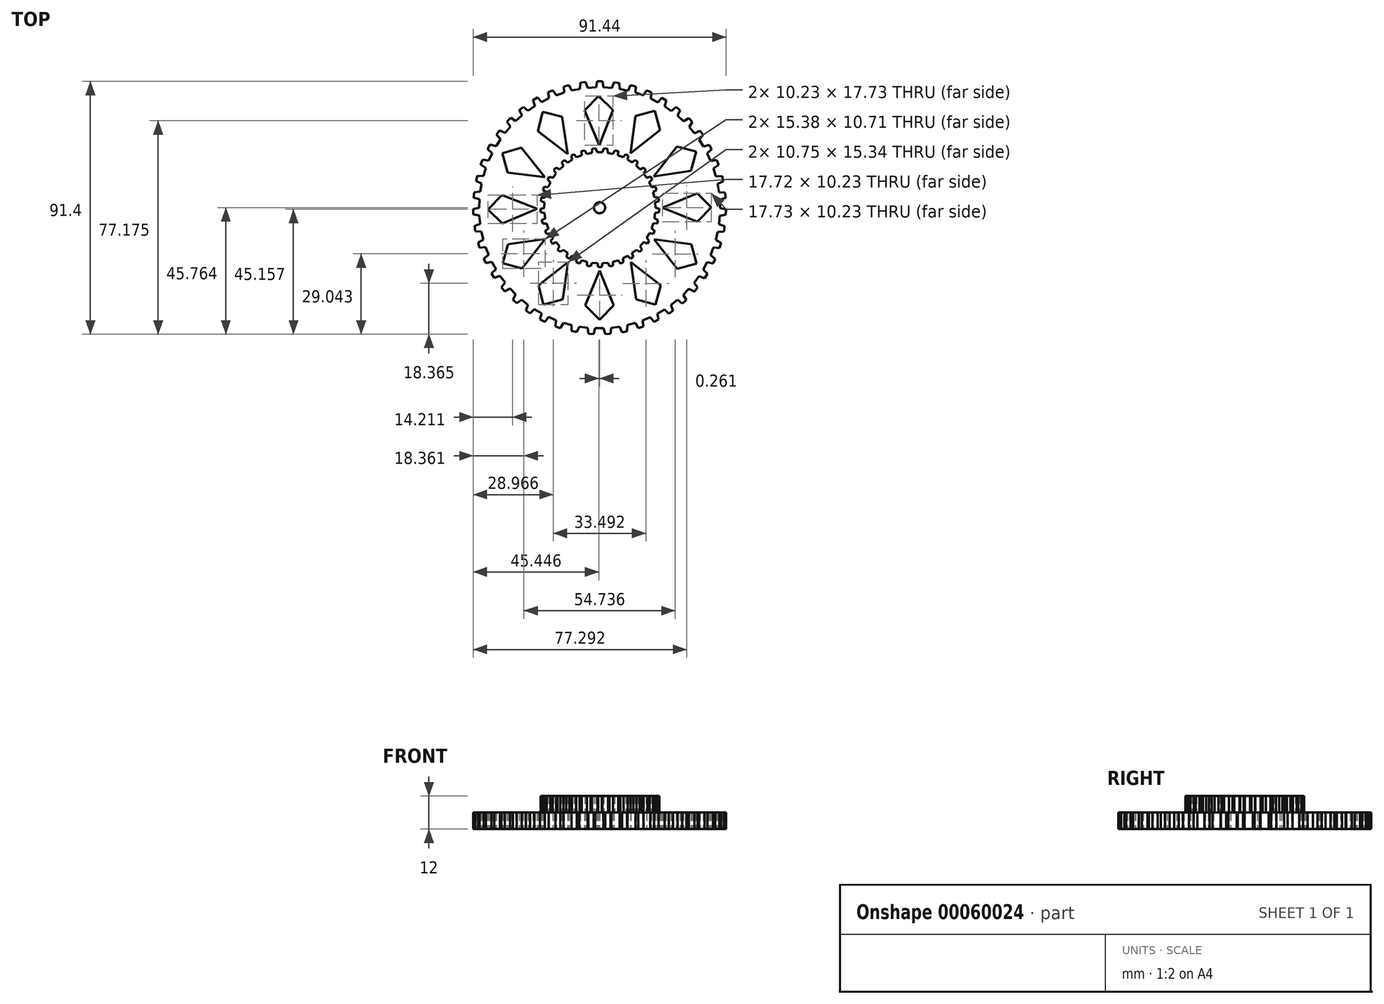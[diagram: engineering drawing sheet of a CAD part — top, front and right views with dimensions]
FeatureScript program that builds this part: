
annotation { "Feature Type Name" : "Feature", "Feature Type Description" : "" }
export const myFeature = defineFeature(function(context is Context, id is Id, definition is map)
    precondition{}
    {
        {
            var Q0;
            Q0=qCreatedBy(makeId("Top.planeOp"),FACE);
            var sketch = newSketch(context, id + "F0", { "sketchPlane" : qUnion([Q0])});
            skLineSegment(sketch, "E0", {"start": v(20.19, -0.05) * mm, "end": v(20.1, 1.94) * mm});
            skLineSegment(sketch, "E1", {"start": v(20.1, 1.94) * mm, "end": v(21.44, 2.42) * mm});
            skLineSegment(sketch, "E2", {"start": v(21.44, 2.42) * mm, "end": v(21.26, 3.68) * mm});
            skLineSegment(sketch, "E3", {"start": v(21.26, 3.68) * mm, "end": v(19.83, 3.76) * mm});
            skLineSegment(sketch, "E4", {"start": v(19.83, 3.76) * mm, "end": v(19.37, 5.7) * mm});
            skLineSegment(sketch, "E5", {"start": v(19.37, 5.7) * mm, "end": v(20.6, 6.42) * mm});
            skLineSegment(sketch, "E6", {"start": v(20.6, 6.42) * mm, "end": v(20.18, 7.62) * mm});
            skLineSegment(sketch, "E7", {"start": v(20.18, 7.62) * mm, "end": v(18.77, 7.43) * mm});
            skLineSegment(sketch, "E8", {"start": v(18.77, 7.43) * mm, "end": v(17.94, 9.24) * mm});
            skLineSegment(sketch, "E9", {"start": v(17.94, 9.24) * mm, "end": v(19, 10.18) * mm});
            skLineSegment(sketch, "E10", {"start": v(19, 10.18) * mm, "end": v(18.37, 11.28) * mm});
            skLineSegment(sketch, "E11", {"start": v(18.37, 11.28) * mm, "end": v(17.02, 10.82) * mm});
            skLineSegment(sketch, "E12", {"start": v(17.02, 10.82) * mm, "end": v(15.86, 12.44) * mm});
            skLineSegment(sketch, "E13", {"start": v(15.86, 12.44) * mm, "end": v(16.73, 13.57) * mm});
            skLineSegment(sketch, "E14", {"start": v(16.73, 13.57) * mm, "end": v(15.9, 14.53) * mm});
            skLineSegment(sketch, "E15", {"start": v(15.9, 14.53) * mm, "end": v(14.66, 13.83) * mm});
            skLineSegment(sketch, "E16", {"start": v(14.66, 13.83) * mm, "end": v(13.21, 15.2) * mm});
            skLineSegment(sketch, "E17", {"start": v(13.21, 15.2) * mm, "end": v(13.85, 16.47) * mm});
            skLineSegment(sketch, "E18", {"start": v(13.85, 16.47) * mm, "end": v(12.86, 17.26) * mm});
            skLineSegment(sketch, "E19", {"start": v(12.86, 17.26) * mm, "end": v(11.77, 16.34) * mm});
            skLineSegment(sketch, "E20", {"start": v(11.77, 16.34) * mm, "end": v(10.1, 17.41) * mm});
            skLineSegment(sketch, "E21", {"start": v(10.1, 17.41) * mm, "end": v(10.49, 18.78) * mm});
            skLineSegment(sketch, "E22", {"start": v(10.49, 18.78) * mm, "end": v(9.36, 19.36) * mm});
            skLineSegment(sketch, "E23", {"start": v(9.36, 19.36) * mm, "end": v(8.47, 18.25) * mm});
            skLineSegment(sketch, "E24", {"start": v(8.47, 18.25) * mm, "end": v(6.62, 19) * mm});
            skLineSegment(sketch, "E25", {"start": v(6.62, 19) * mm, "end": v(6.74, 20.41) * mm});
            skLineSegment(sketch, "E26", {"start": v(6.74, 20.41) * mm, "end": v(5.52, 20.77) * mm});
            skLineSegment(sketch, "E27", {"start": v(5.52, 20.77) * mm, "end": v(4.86, 19.5) * mm});
            skLineSegment(sketch, "E28", {"start": v(4.86, 19.5) * mm, "end": v(2.9, 19.88) * mm});
            skLineSegment(sketch, "E29", {"start": v(2.9, 19.88) * mm, "end": v(2.75, 21.3) * mm});
            skLineSegment(sketch, "E30", {"start": v(2.75, 21.3) * mm, "end": v(1.49, 21.41) * mm});
            skLineSegment(sketch, "E31", {"start": v(1.49, 21.41) * mm, "end": v(1.07, 20.04) * mm});
            skLineSegment(sketch, "E32", {"start": v(1.07, 20.04) * mm, "end": v(-0.92, 20.04) * mm});
            skLineSegment(sketch, "E33", {"start": v(-0.92, 20.04) * mm, "end": v(-1.33, 21.41) * mm});
            skLineSegment(sketch, "E34", {"start": v(-1.33, 21.41) * mm, "end": v(-2.6, 21.3) * mm});
            skLineSegment(sketch, "E35", {"start": v(-2.6, 21.3) * mm, "end": v(-2.74, 19.87) * mm});
            skLineSegment(sketch, "E36", {"start": v(-2.74, 19.87) * mm, "end": v(-4.7, 19.5) * mm});
            skLineSegment(sketch, "E37", {"start": v(-4.7, 19.5) * mm, "end": v(-5.36, 20.76) * mm});
            skLineSegment(sketch, "E38", {"start": v(-5.36, 20.76) * mm, "end": v(-6.58, 20.4) * mm});
            skLineSegment(sketch, "E39", {"start": v(-6.58, 20.4) * mm, "end": v(-6.46, 18.98) * mm});
            skLineSegment(sketch, "E40", {"start": v(-6.46, 18.98) * mm, "end": v(-8.3, 18.24) * mm});
            skLineSegment(sketch, "E41", {"start": v(-8.3, 18.24) * mm, "end": v(-9.2, 19.35) * mm});
            skLineSegment(sketch, "E42", {"start": v(-9.2, 19.35) * mm, "end": v(-10.33, 18.76) * mm});
            skLineSegment(sketch, "E43", {"start": v(-10.33, 18.76) * mm, "end": v(-9.93, 17.4) * mm});
            skLineSegment(sketch, "E44", {"start": v(-9.93, 17.4) * mm, "end": v(-11.6, 16.31) * mm});
            skLineSegment(sketch, "E45", {"start": v(-11.6, 16.31) * mm, "end": v(-12.7, 17.23) * mm});
            skLineSegment(sketch, "E46", {"start": v(-12.7, 17.23) * mm, "end": v(-13.7, 16.45) * mm});
            skLineSegment(sketch, "E47", {"start": v(-13.7, 16.45) * mm, "end": v(-13.05, 15.18) * mm});
            skLineSegment(sketch, "E48", {"start": v(-13.05, 15.18) * mm, "end": v(-14.49, 13.8) * mm});
            skLineSegment(sketch, "E49", {"start": v(-14.49, 13.8) * mm, "end": v(-15.73, 14.5) * mm});
            skLineSegment(sketch, "E50", {"start": v(-15.73, 14.5) * mm, "end": v(-16.56, 13.54) * mm});
            skLineSegment(sketch, "E51", {"start": v(-16.56, 13.54) * mm, "end": v(-15.69, 12.42) * mm});
            skLineSegment(sketch, "E52", {"start": v(-15.69, 12.42) * mm, "end": v(-16.84, 10.8) * mm});
            skLineSegment(sketch, "E53", {"start": v(-16.84, 10.8) * mm, "end": v(-18.2, 11.25) * mm});
            skLineSegment(sketch, "E54", {"start": v(-18.2, 11.25) * mm, "end": v(-18.83, 10.15) * mm});
            skLineSegment(sketch, "E55", {"start": v(-18.83, 10.15) * mm, "end": v(-17.76, 9.2) * mm});
            skLineSegment(sketch, "E56", {"start": v(-17.76, 9.2) * mm, "end": v(-18.59, 7.4) * mm});
            skLineSegment(sketch, "E57", {"start": v(-18.59, 7.4) * mm, "end": v(-20, 7.58) * mm});
            skLineSegment(sketch, "E58", {"start": v(-20, 7.58) * mm, "end": v(-20.41, 6.38) * mm});
            skLineSegment(sketch, "E59", {"start": v(-20.41, 6.38) * mm, "end": v(-19.18, 5.66) * mm});
            skLineSegment(sketch, "E60", {"start": v(-19.18, 5.66) * mm, "end": v(-19.65, 3.72) * mm});
            skLineSegment(sketch, "E61", {"start": v(-19.65, 3.72) * mm, "end": v(-21.08, 3.64) * mm});
            skLineSegment(sketch, "E62", {"start": v(-21.08, 3.64) * mm, "end": v(-21.25, 2.38) * mm});
            skLineSegment(sketch, "E63", {"start": v(-21.25, 2.38) * mm, "end": v(-19.9, 1.9) * mm});
            skLineSegment(sketch, "E64", {"start": v(-19.9, 1.9) * mm, "end": v(-20, -0.08) * mm});
            skLineSegment(sketch, "E65", {"start": v(-20, -0.08) * mm, "end": v(-21.38, -0.43) * mm});
            skLineSegment(sketch, "E66", {"start": v(-21.38, -0.43) * mm, "end": v(-21.32, -1.7) * mm});
            skLineSegment(sketch, "E67", {"start": v(-21.32, -1.7) * mm, "end": v(-19.9, -1.91) * mm});
            skLineSegment(sketch, "E68", {"start": v(-19.9, -1.91) * mm, "end": v(-19.62, -3.88) * mm});
            skLineSegment(sketch, "E69", {"start": v(-19.62, -3.88) * mm, "end": v(-20.92, -4.49) * mm});
            skLineSegment(sketch, "E70", {"start": v(-20.92, -4.49) * mm, "end": v(-20.62, -5.72) * mm});
            skLineSegment(sketch, "E71", {"start": v(-20.62, -5.72) * mm, "end": v(-19.2, -5.67) * mm});
            skLineSegment(sketch, "E72", {"start": v(-19.2, -5.67) * mm, "end": v(-18.54, -7.55) * mm});
            skLineSegment(sketch, "E73", {"start": v(-18.54, -7.55) * mm, "end": v(-19.7, -8.39) * mm});
            skLineSegment(sketch, "E74", {"start": v(-19.7, -8.39) * mm, "end": v(-19.17, -9.54) * mm});
            skLineSegment(sketch, "E75", {"start": v(-19.17, -9.54) * mm, "end": v(-17.78, -9.22) * mm});
            skLineSegment(sketch, "E76", {"start": v(-17.78, -9.22) * mm, "end": v(-16.78, -10.94) * mm});
            skLineSegment(sketch, "E77", {"start": v(-16.78, -10.94) * mm, "end": v(-17.75, -11.98) * mm});
            skLineSegment(sketch, "E78", {"start": v(-17.75, -11.98) * mm, "end": v(-17.01, -13.01) * mm});
            skLineSegment(sketch, "E79", {"start": v(-17.01, -13.01) * mm, "end": v(-15.71, -12.43) * mm});
            skLineSegment(sketch, "E80", {"start": v(-15.71, -12.43) * mm, "end": v(-14.4, -13.93) * mm});
            skLineSegment(sketch, "E81", {"start": v(-14.4, -13.93) * mm, "end": v(-15.17, -15.14) * mm});
            skLineSegment(sketch, "E82", {"start": v(-15.17, -15.14) * mm, "end": v(-14.25, -16.02) * mm});
            skLineSegment(sketch, "E83", {"start": v(-14.25, -16.02) * mm, "end": v(-13.08, -15.2) * mm});
            skLineSegment(sketch, "E84", {"start": v(-13.08, -15.2) * mm, "end": v(-11.51, -16.43) * mm});
            skLineSegment(sketch, "E85", {"start": v(-11.51, -16.43) * mm, "end": v(-12.03, -17.76) * mm});
            skLineSegment(sketch, "E86", {"start": v(-12.03, -17.76) * mm, "end": v(-10.96, -18.44) * mm});
            skLineSegment(sketch, "E87", {"start": v(-10.96, -18.44) * mm, "end": v(-9.97, -17.42) * mm});
            skLineSegment(sketch, "E88", {"start": v(-9.97, -17.42) * mm, "end": v(-8.2, -18.33) * mm});
            skLineSegment(sketch, "E89", {"start": v(-8.2, -18.33) * mm, "end": v(-8.46, -19.74) * mm});
            skLineSegment(sketch, "E90", {"start": v(-8.46, -19.74) * mm, "end": v(-7.28, -20.2) * mm});
            skLineSegment(sketch, "E91", {"start": v(-7.28, -20.2) * mm, "end": v(-6.5, -19.01) * mm});
            skLineSegment(sketch, "E92", {"start": v(-6.5, -19.01) * mm, "end": v(-4.59, -19.57) * mm});
            skLineSegment(sketch, "E93", {"start": v(-4.59, -19.57) * mm, "end": v(-4.57, -21) * mm});
            skLineSegment(sketch, "E94", {"start": v(-4.57, -21) * mm, "end": v(-3.32, -21.23) * mm});
            skLineSegment(sketch, "E95", {"start": v(-3.32, -21.23) * mm, "end": v(-2.78, -19.91) * mm});
            skLineSegment(sketch, "E96", {"start": v(-2.78, -19.91) * mm, "end": v(-0.8, -20.1) * mm});
            skLineSegment(sketch, "E97", {"start": v(-0.8, -20.1) * mm, "end": v(-0.52, -21.5) * mm});
            skLineSegment(sketch, "E98", {"start": v(-0.52, -21.5) * mm, "end": v(0.75, -21.5) * mm});
            skLineSegment(sketch, "E99", {"start": v(0.75, -21.5) * mm, "end": v(1.03, -20.1) * mm});
            skLineSegment(sketch, "E100", {"start": v(1.03, -20.1) * mm, "end": v(3.01, -19.9) * mm});
            skLineSegment(sketch, "E101", {"start": v(3.01, -19.9) * mm, "end": v(3.56, -21.23) * mm});
            skLineSegment(sketch, "E102", {"start": v(3.56, -21.23) * mm, "end": v(4.8, -21) * mm});
            skLineSegment(sketch, "E103", {"start": v(4.8, -21) * mm, "end": v(4.82, -19.56) * mm});
            skLineSegment(sketch, "E104", {"start": v(4.82, -19.56) * mm, "end": v(6.73, -19) * mm});
            skLineSegment(sketch, "E105", {"start": v(6.73, -19) * mm, "end": v(7.5, -20.2) * mm});
            skLineSegment(sketch, "E106", {"start": v(7.5, -20.2) * mm, "end": v(8.69, -19.72) * mm});
            skLineSegment(sketch, "E107", {"start": v(8.69, -19.72) * mm, "end": v(8.43, -18.32) * mm});
            skLineSegment(sketch, "E108", {"start": v(8.43, -18.32) * mm, "end": v(10.2, -17.4) * mm});
            skLineSegment(sketch, "E109", {"start": v(10.2, -17.4) * mm, "end": v(11.2, -18.42) * mm});
            skLineSegment(sketch, "E110", {"start": v(11.2, -18.42) * mm, "end": v(12.26, -17.74) * mm});
            skLineSegment(sketch, "E111", {"start": v(12.26, -17.74) * mm, "end": v(11.74, -16.4) * mm});
            skLineSegment(sketch, "E112", {"start": v(11.74, -16.4) * mm, "end": v(13.3, -15.17) * mm});
            skLineSegment(sketch, "E113", {"start": v(13.3, -15.17) * mm, "end": v(14.47, -15.99) * mm});
            skLineSegment(sketch, "E114", {"start": v(14.47, -15.99) * mm, "end": v(15.39, -15.11) * mm});
            skLineSegment(sketch, "E115", {"start": v(15.39, -15.11) * mm, "end": v(14.63, -13.9) * mm});
            skLineSegment(sketch, "E116", {"start": v(14.63, -13.9) * mm, "end": v(15.93, -12.4) * mm});
            skLineSegment(sketch, "E117", {"start": v(15.93, -12.4) * mm, "end": v(17.23, -12.98) * mm});
            skLineSegment(sketch, "E118", {"start": v(17.23, -12.98) * mm, "end": v(17.97, -11.95) * mm});
            skLineSegment(sketch, "E119", {"start": v(17.97, -11.95) * mm, "end": v(17, -10.9) * mm});
            skLineSegment(sketch, "E120", {"start": v(17, -10.9) * mm, "end": v(18, -9.18) * mm});
            skLineSegment(sketch, "E121", {"start": v(18, -9.18) * mm, "end": v(19.38, -9.5) * mm});
            skLineSegment(sketch, "E122", {"start": v(19.38, -9.5) * mm, "end": v(19.9, -8.35) * mm});
            skLineSegment(sketch, "E123", {"start": v(19.9, -8.35) * mm, "end": v(18.75, -7.51) * mm});
            skLineSegment(sketch, "E124", {"start": v(18.75, -7.51) * mm, "end": v(19.4, -5.63) * mm});
            skLineSegment(sketch, "E125", {"start": v(19.4, -5.63) * mm, "end": v(20.83, -5.69) * mm});
            skLineSegment(sketch, "E126", {"start": v(20.83, -5.69) * mm, "end": v(21.12, -4.45) * mm});
            skLineSegment(sketch, "E127", {"start": v(21.12, -4.45) * mm, "end": v(19.83, -3.85) * mm});
            skLineSegment(sketch, "E128", {"start": v(19.83, -3.85) * mm, "end": v(20.1, -1.88) * mm});
            skLineSegment(sketch, "E129", {"start": v(20.1, -1.88) * mm, "end": v(21.52, -1.66) * mm});
            skLineSegment(sketch, "E130", {"start": v(21.52, -1.66) * mm, "end": v(21.58, -0.4) * mm});
            skLineSegment(sketch, "E131", {"start": v(21.58, -0.4) * mm, "end": v(20.19, -0.05) * mm});
            skLineSegment(sketch, "E132", {"start": v(-22.65, -0.36) * mm, "end": v(-35.18, -5.66) * mm});
            skLineSegment(sketch, "E133", {"start": v(-35.18, -5.66) * mm, "end": v(-40.37, -0.62) * mm});
            skLineSegment(sketch, "E134", {"start": v(-40.37, -0.62) * mm, "end": v(-35.33, 4.57) * mm});
            skLineSegment(sketch, "E135", {"start": v(-35.33, 4.57) * mm, "end": v(-22.65, -0.36) * mm});
            skLineSegment(sketch, "E136", {"start": v(-19.74, 11.05) * mm, "end": v(-33.24, 12.75) * mm});
            skLineSegment(sketch, "E137", {"start": v(-33.24, 12.75) * mm, "end": v(-35.2, 19.71) * mm});
            skLineSegment(sketch, "E138", {"start": v(-35.2, 19.71) * mm, "end": v(-28.24, 21.68) * mm});
            skLineSegment(sketch, "E139", {"start": v(-28.24, 21.68) * mm, "end": v(-19.74, 11.05) * mm});
            skLineSegment(sketch, "E140", {"start": v(-11.5, 19.47) * mm, "end": v(-22.33, 27.7) * mm});
            skLineSegment(sketch, "E141", {"start": v(-22.33, 27.7) * mm, "end": v(-20.54, 34.71) * mm});
            skLineSegment(sketch, "E142", {"start": v(-20.54, 34.71) * mm, "end": v(-13.53, 32.92) * mm});
            skLineSegment(sketch, "E143", {"start": v(-13.53, 32.92) * mm, "end": v(-11.5, 19.47) * mm});
            skLineSegment(sketch, "E144", {"start": v(-0.15, 22.61) * mm, "end": v(-5.39, 35.17) * mm});
            skLineSegment(sketch, "E145", {"start": v(-5.39, 35.17) * mm, "end": v(-0.32, 40.34) * mm});
            skLineSegment(sketch, "E146", {"start": v(-0.32, 40.34) * mm, "end": v(4.84, 35.28) * mm});
            skLineSegment(sketch, "E147", {"start": v(4.84, 35.28) * mm, "end": v(-0.15, 22.61) * mm});
            skLineSegment(sketch, "E148", {"start": v(11.25, 19.64) * mm, "end": v(13.01, 33.14) * mm});
            skLineSegment(sketch, "E149", {"start": v(13.01, 33.14) * mm, "end": v(19.98, 35.07) * mm});
            skLineSegment(sketch, "E150", {"start": v(19.98, 35.07) * mm, "end": v(21.91, 28.1) * mm});
            skLineSegment(sketch, "E151", {"start": v(21.91, 28.1) * mm, "end": v(11.25, 19.64) * mm});
            skLineSegment(sketch, "E152", {"start": v(19.62, 11.36) * mm, "end": v(27.91, 22.15) * mm});
            skLineSegment(sketch, "E153", {"start": v(27.91, 22.15) * mm, "end": v(34.91, 20.33) * mm});
            skLineSegment(sketch, "E154", {"start": v(34.91, 20.33) * mm, "end": v(33.09, 13.33) * mm});
            skLineSegment(sketch, "E155", {"start": v(33.09, 13.33) * mm, "end": v(19.62, 11.36) * mm});
            skLineSegment(sketch, "E156", {"start": v(22.7, 0) * mm, "end": v(35.3, 5.18) * mm});
            skLineSegment(sketch, "E157", {"start": v(35.3, 5.18) * mm, "end": v(40.44, 0.1) * mm});
            skLineSegment(sketch, "E158", {"start": v(40.44, 0.1) * mm, "end": v(35.35, -5.05) * mm});
            skLineSegment(sketch, "E159", {"start": v(35.35, -5.05) * mm, "end": v(22.7, 0) * mm});
            skLineSegment(sketch, "E160", {"start": v(19.69, -11.38) * mm, "end": v(33.17, -13.21) * mm});
            skLineSegment(sketch, "E161", {"start": v(33.17, -13.21) * mm, "end": v(35.07, -20.2) * mm});
            skLineSegment(sketch, "E162", {"start": v(35.07, -20.2) * mm, "end": v(28.09, -22.09) * mm});
            skLineSegment(sketch, "E163", {"start": v(28.09, -22.09) * mm, "end": v(19.69, -11.38) * mm});
            skLineSegment(sketch, "E164", {"start": v(11.36, -19.71) * mm, "end": v(22.11, -28.06) * mm});
            skLineSegment(sketch, "E165", {"start": v(22.11, -28.06) * mm, "end": v(20.25, -35.05) * mm});
            skLineSegment(sketch, "E166", {"start": v(20.25, -35.05) * mm, "end": v(13.26, -33.19) * mm});
            skLineSegment(sketch, "E167", {"start": v(13.26, -33.19) * mm, "end": v(11.36, -19.71) * mm});
            skLineSegment(sketch, "E168", {"start": v(-0.01, -22.75) * mm, "end": v(5.1, -35.36) * mm});
            skLineSegment(sketch, "E169", {"start": v(5.1, -35.36) * mm, "end": v(-0.01, -40.47) * mm});
            skLineSegment(sketch, "E170", {"start": v(-0.01, -40.47) * mm, "end": v(-5.13, -35.36) * mm});
            skLineSegment(sketch, "E171", {"start": v(-5.13, -35.36) * mm, "end": v(-0.01, -22.75) * mm});
            skLineSegment(sketch, "E172", {"start": v(-11.38, -19.67) * mm, "end": v(-13.28, -33.14) * mm});
            skLineSegment(sketch, "E173", {"start": v(-13.28, -33.14) * mm, "end": v(-20.27, -35) * mm});
            skLineSegment(sketch, "E174", {"start": v(-20.27, -35) * mm, "end": v(-22.13, -28.02) * mm});
            skLineSegment(sketch, "E175", {"start": v(-22.13, -28.02) * mm, "end": v(-11.38, -19.67) * mm});
            skLineSegment(sketch, "E176", {"start": v(-19.67, -11.3) * mm, "end": v(-28.07, -22.01) * mm});
            skLineSegment(sketch, "E177", {"start": v(-28.07, -22.01) * mm, "end": v(-35.05, -20.12) * mm});
            skLineSegment(sketch, "E178", {"start": v(-35.05, -20.12) * mm, "end": v(-33.16, -13.14) * mm});
            skLineSegment(sketch, "E179", {"start": v(-33.16, -13.14) * mm, "end": v(-19.67, -11.3) * mm});
            skLineSegment(sketch, "E180", {"start": v(43.6, -0.15) * mm, "end": v(43.5, 2.88) * mm});
            skLineSegment(sketch, "E181", {"start": v(43.5, 2.88) * mm, "end": v(45.6, 3.54) * mm});
            skLineSegment(sketch, "E182", {"start": v(45.6, 3.54) * mm, "end": v(45.41, 5.42) * mm});
            skLineSegment(sketch, "E183", {"start": v(45.41, 5.42) * mm, "end": v(43.23, 5.66) * mm});
            skLineSegment(sketch, "E184", {"start": v(43.23, 5.66) * mm, "end": v(42.73, 8.66) * mm});
            skLineSegment(sketch, "E185", {"start": v(42.73, 8.66) * mm, "end": v(44.72, 9.58) * mm});
            skLineSegment(sketch, "E186", {"start": v(44.72, 9.58) * mm, "end": v(44.28, 11.43) * mm});
            skLineSegment(sketch, "E187", {"start": v(44.28, 11.43) * mm, "end": v(42.1, 11.37) * mm});
            skLineSegment(sketch, "E188", {"start": v(42.1, 11.37) * mm, "end": v(41.2, 14.28) * mm});
            skLineSegment(sketch, "E189", {"start": v(41.2, 14.28) * mm, "end": v(43.04, 15.46) * mm});
            skLineSegment(sketch, "E190", {"start": v(43.04, 15.46) * mm, "end": v(42.36, 17.23) * mm});
            skLineSegment(sketch, "E191", {"start": v(42.36, 17.23) * mm, "end": v(40.2, 16.88) * mm});
            skLineSegment(sketch, "E192", {"start": v(40.2, 16.88) * mm, "end": v(38.92, 19.63) * mm});
            skLineSegment(sketch, "E193", {"start": v(38.92, 19.63) * mm, "end": v(40.59, 21.06) * mm});
            skLineSegment(sketch, "E194", {"start": v(40.59, 21.06) * mm, "end": v(39.68, 22.72) * mm});
            skLineSegment(sketch, "E195", {"start": v(39.68, 22.72) * mm, "end": v(37.59, 22.08) * mm});
            skLineSegment(sketch, "E196", {"start": v(37.59, 22.08) * mm, "end": v(35.95, 24.64) * mm});
            skLineSegment(sketch, "E197", {"start": v(35.95, 24.64) * mm, "end": v(37.42, 26.28) * mm});
            skLineSegment(sketch, "E198", {"start": v(37.42, 26.28) * mm, "end": v(36.3, 27.8) * mm});
            skLineSegment(sketch, "E199", {"start": v(36.3, 27.8) * mm, "end": v(34.3, 26.9) * mm});
            skLineSegment(sketch, "E200", {"start": v(34.3, 26.9) * mm, "end": v(32.34, 29.21) * mm});
            skLineSegment(sketch, "E201", {"start": v(32.34, 29.21) * mm, "end": v(33.58, 31.03) * mm});
            skLineSegment(sketch, "E202", {"start": v(33.58, 31.03) * mm, "end": v(32.26, 32.39) * mm});
            skLineSegment(sketch, "E203", {"start": v(32.26, 32.39) * mm, "end": v(30.4, 31.22) * mm});
            skLineSegment(sketch, "E204", {"start": v(30.4, 31.22) * mm, "end": v(28.15, 33.26) * mm});
            skLineSegment(sketch, "E205", {"start": v(28.15, 33.26) * mm, "end": v(29.14, 35.22) * mm});
            skLineSegment(sketch, "E206", {"start": v(29.14, 35.22) * mm, "end": v(27.65, 36.4) * mm});
            skLineSegment(sketch, "E207", {"start": v(27.65, 36.4) * mm, "end": v(25.97, 35) * mm});
            skLineSegment(sketch, "E208", {"start": v(25.97, 35) * mm, "end": v(23.47, 36.72) * mm});
            skLineSegment(sketch, "E209", {"start": v(23.47, 36.72) * mm, "end": v(24.18, 38.8) * mm});
            skLineSegment(sketch, "E210", {"start": v(24.18, 38.8) * mm, "end": v(22.55, 39.76) * mm});
            skLineSegment(sketch, "E211", {"start": v(22.55, 39.76) * mm, "end": v(21.07, 38.15) * mm});
            skLineSegment(sketch, "E212", {"start": v(21.07, 38.15) * mm, "end": v(18.37, 39.53) * mm});
            skLineSegment(sketch, "E213", {"start": v(18.37, 39.53) * mm, "end": v(18.8, 41.67) * mm});
            skLineSegment(sketch, "E214", {"start": v(18.8, 41.67) * mm, "end": v(17.05, 42.42) * mm});
            skLineSegment(sketch, "E215", {"start": v(17.05, 42.42) * mm, "end": v(15.8, 40.62) * mm});
            skLineSegment(sketch, "E216", {"start": v(15.8, 40.62) * mm, "end": v(12.93, 41.62) * mm});
            skLineSegment(sketch, "E217", {"start": v(12.93, 41.62) * mm, "end": v(13.07, 43.82) * mm});
            skLineSegment(sketch, "E218", {"start": v(13.07, 43.82) * mm, "end": v(11.24, 44.31) * mm});
            skLineSegment(sketch, "E219", {"start": v(11.24, 44.31) * mm, "end": v(10.24, 42.36) * mm});
            skLineSegment(sketch, "E220", {"start": v(10.24, 42.36) * mm, "end": v(7.26, 42.97) * mm});
            skLineSegment(sketch, "E221", {"start": v(7.26, 42.97) * mm, "end": v(7.1, 45.15) * mm});
            skLineSegment(sketch, "E222", {"start": v(7.1, 45.15) * mm, "end": v(5.23, 45.4) * mm});
            skLineSegment(sketch, "E223", {"start": v(5.23, 45.4) * mm, "end": v(4.5, 43.34) * mm});
            skLineSegment(sketch, "E224", {"start": v(4.5, 43.34) * mm, "end": v(1.47, 43.55) * mm});
            skLineSegment(sketch, "E225", {"start": v(1.47, 43.55) * mm, "end": v(1.02, 45.69) * mm});
            skLineSegment(sketch, "E226", {"start": v(1.02, 45.69) * mm, "end": v(-0.87, 45.7) * mm});
            skLineSegment(sketch, "E227", {"start": v(-0.87, 45.7) * mm, "end": v(-1.32, 43.55) * mm});
            skLineSegment(sketch, "E228", {"start": v(-1.32, 43.55) * mm, "end": v(-4.35, 43.35) * mm});
            skLineSegment(sketch, "E229", {"start": v(-4.35, 43.35) * mm, "end": v(-5.08, 45.43) * mm});
            skLineSegment(sketch, "E230", {"start": v(-5.08, 45.43) * mm, "end": v(-6.95, 45.17) * mm});
            skLineSegment(sketch, "E231", {"start": v(-6.95, 45.17) * mm, "end": v(-7.12, 42.99) * mm});
            skLineSegment(sketch, "E232", {"start": v(-7.12, 42.99) * mm, "end": v(-10.1, 42.4) * mm});
            skLineSegment(sketch, "E233", {"start": v(-10.1, 42.4) * mm, "end": v(-11.09, 44.34) * mm});
            skLineSegment(sketch, "E234", {"start": v(-11.09, 44.34) * mm, "end": v(-12.92, 43.84) * mm});
            skLineSegment(sketch, "E235", {"start": v(-12.92, 43.84) * mm, "end": v(-12.79, 41.66) * mm});
            skLineSegment(sketch, "E236", {"start": v(-12.79, 41.66) * mm, "end": v(-15.66, 40.67) * mm});
            skLineSegment(sketch, "E237", {"start": v(-15.66, 40.67) * mm, "end": v(-16.9, 42.47) * mm});
            skLineSegment(sketch, "E238", {"start": v(-16.9, 42.47) * mm, "end": v(-18.65, 41.74) * mm});
            skLineSegment(sketch, "E239", {"start": v(-18.65, 41.74) * mm, "end": v(-18.23, 39.58) * mm});
            skLineSegment(sketch, "E240", {"start": v(-18.23, 39.58) * mm, "end": v(-20.94, 38.21) * mm});
            skLineSegment(sketch, "E241", {"start": v(-20.94, 38.21) * mm, "end": v(-22.42, 39.84) * mm});
            skLineSegment(sketch, "E242", {"start": v(-22.42, 39.84) * mm, "end": v(-24.05, 38.87) * mm});
            skLineSegment(sketch, "E243", {"start": v(-24.05, 38.87) * mm, "end": v(-23.34, 36.8) * mm});
            skLineSegment(sketch, "E244", {"start": v(-23.34, 36.8) * mm, "end": v(-25.85, 35.08) * mm});
            skLineSegment(sketch, "E245", {"start": v(-25.85, 35.08) * mm, "end": v(-27.53, 36.49) * mm});
            skLineSegment(sketch, "E246", {"start": v(-27.53, 36.49) * mm, "end": v(-29.01, 35.31) * mm});
            skLineSegment(sketch, "E247", {"start": v(-29.01, 35.31) * mm, "end": v(-28.04, 33.35) * mm});
            skLineSegment(sketch, "E248", {"start": v(-28.04, 33.35) * mm, "end": v(-30.3, 31.32) * mm});
            skLineSegment(sketch, "E249", {"start": v(-30.3, 31.32) * mm, "end": v(-32.14, 32.49) * mm});
            skLineSegment(sketch, "E250", {"start": v(-32.14, 32.49) * mm, "end": v(-33.46, 31.13) * mm});
            skLineSegment(sketch, "E251", {"start": v(-33.46, 31.13) * mm, "end": v(-32.24, 29.31) * mm});
            skLineSegment(sketch, "E252", {"start": v(-32.24, 29.31) * mm, "end": v(-34.2, 27) * mm});
            skLineSegment(sketch, "E253", {"start": v(-34.2, 27) * mm, "end": v(-36.19, 27.91) * mm});
            skLineSegment(sketch, "E254", {"start": v(-36.19, 27.91) * mm, "end": v(-37.32, 26.4) * mm});
            skLineSegment(sketch, "E255", {"start": v(-37.32, 26.4) * mm, "end": v(-35.86, 24.76) * mm});
            skLineSegment(sketch, "E256", {"start": v(-35.86, 24.76) * mm, "end": v(-37.5, 22.2) * mm});
            skLineSegment(sketch, "E257", {"start": v(-37.5, 22.2) * mm, "end": v(-39.6, 22.85) * mm});
            skLineSegment(sketch, "E258", {"start": v(-39.6, 22.85) * mm, "end": v(-40.52, 21.19) * mm});
            skLineSegment(sketch, "E259", {"start": v(-40.52, 21.19) * mm, "end": v(-38.85, 19.76) * mm});
            skLineSegment(sketch, "E260", {"start": v(-38.85, 19.76) * mm, "end": v(-40.13, 17) * mm});
            skLineSegment(sketch, "E261", {"start": v(-40.13, 17) * mm, "end": v(-42.3, 17.36) * mm});
            skLineSegment(sketch, "E262", {"start": v(-42.3, 17.36) * mm, "end": v(-42.98, 15.6) * mm});
            skLineSegment(sketch, "E263", {"start": v(-42.98, 15.6) * mm, "end": v(-41.14, 14.4) * mm});
            skLineSegment(sketch, "E264", {"start": v(-41.14, 14.4) * mm, "end": v(-42.05, 11.5) * mm});
            skLineSegment(sketch, "E265", {"start": v(-42.05, 11.5) * mm, "end": v(-44.23, 11.57) * mm});
            skLineSegment(sketch, "E266", {"start": v(-44.23, 11.57) * mm, "end": v(-44.67, 9.72) * mm});
            skLineSegment(sketch, "E267", {"start": v(-44.67, 9.72) * mm, "end": v(-42.7, 8.79) * mm});
            skLineSegment(sketch, "E268", {"start": v(-42.7, 8.79) * mm, "end": v(-43.2, 5.8) * mm});
            skLineSegment(sketch, "E269", {"start": v(-43.2, 5.8) * mm, "end": v(-45.38, 5.57) * mm});
            skLineSegment(sketch, "E270", {"start": v(-45.38, 5.57) * mm, "end": v(-45.57, 3.68) * mm});
            skLineSegment(sketch, "E271", {"start": v(-45.57, 3.68) * mm, "end": v(-43.48, 3.02) * mm});
            skLineSegment(sketch, "E272", {"start": v(-43.48, 3.02) * mm, "end": v(-43.58, -0.02) * mm});
            skLineSegment(sketch, "E273", {"start": v(-43.58, -0.02) * mm, "end": v(-45.72, -0.53) * mm});
            skLineSegment(sketch, "E274", {"start": v(-45.72, -0.53) * mm, "end": v(-45.65, -2.43) * mm});
            skLineSegment(sketch, "E275", {"start": v(-45.65, -2.43) * mm, "end": v(-43.5, -2.8) * mm});
            skLineSegment(sketch, "E276", {"start": v(-43.5, -2.8) * mm, "end": v(-43.2, -5.83) * mm});
            skLineSegment(sketch, "E277", {"start": v(-43.2, -5.83) * mm, "end": v(-45.24, -6.62) * mm});
            skLineSegment(sketch, "E278", {"start": v(-45.24, -6.62) * mm, "end": v(-44.93, -8.49) * mm});
            skLineSegment(sketch, "E279", {"start": v(-44.93, -8.49) * mm, "end": v(-42.74, -8.58) * mm});
            skLineSegment(sketch, "E280", {"start": v(-42.74, -8.58) * mm, "end": v(-42.05, -11.54) * mm});
            skLineSegment(sketch, "E281", {"start": v(-42.05, -11.54) * mm, "end": v(-43.97, -12.6) * mm});
            skLineSegment(sketch, "E282", {"start": v(-43.97, -12.6) * mm, "end": v(-43.41, -14.4) * mm});
            skLineSegment(sketch, "E283", {"start": v(-43.41, -14.4) * mm, "end": v(-41.23, -14.2) * mm});
            skLineSegment(sketch, "E284", {"start": v(-41.23, -14.2) * mm, "end": v(-40.14, -17.04) * mm});
            skLineSegment(sketch, "E285", {"start": v(-40.14, -17.04) * mm, "end": v(-41.9, -18.35) * mm});
            skLineSegment(sketch, "E286", {"start": v(-41.9, -18.35) * mm, "end": v(-41.1, -20.07) * mm});
            skLineSegment(sketch, "E287", {"start": v(-41.1, -20.07) * mm, "end": v(-38.97, -19.57) * mm});
            skLineSegment(sketch, "E288", {"start": v(-38.97, -19.57) * mm, "end": v(-37.51, -22.24) * mm});
            skLineSegment(sketch, "E289", {"start": v(-37.51, -22.24) * mm, "end": v(-39.08, -23.77) * mm});
            skLineSegment(sketch, "E290", {"start": v(-39.08, -23.77) * mm, "end": v(-38.06, -25.36) * mm});
            skLineSegment(sketch, "E291", {"start": v(-38.06, -25.36) * mm, "end": v(-36, -24.59) * mm});
            skLineSegment(sketch, "E292", {"start": v(-36, -24.59) * mm, "end": v(-34.2, -27.03) * mm});
            skLineSegment(sketch, "E293", {"start": v(-34.2, -27.03) * mm, "end": v(-35.56, -28.76) * mm});
            skLineSegment(sketch, "E294", {"start": v(-35.56, -28.76) * mm, "end": v(-34.34, -30.2) * mm});
            skLineSegment(sketch, "E295", {"start": v(-34.34, -30.2) * mm, "end": v(-32.41, -29.17) * mm});
            skLineSegment(sketch, "E296", {"start": v(-32.41, -29.17) * mm, "end": v(-30.3, -31.35) * mm});
            skLineSegment(sketch, "E297", {"start": v(-30.3, -31.35) * mm, "end": v(-31.41, -33.24) * mm});
            skLineSegment(sketch, "E298", {"start": v(-31.41, -33.24) * mm, "end": v(-30.01, -34.52) * mm});
            skLineSegment(sketch, "E299", {"start": v(-30.01, -34.52) * mm, "end": v(-28.24, -33.23) * mm});
            skLineSegment(sketch, "E300", {"start": v(-28.24, -33.23) * mm, "end": v(-25.86, -35.11) * mm});
            skLineSegment(sketch, "E301", {"start": v(-25.86, -35.11) * mm, "end": v(-26.71, -37.14) * mm});
            skLineSegment(sketch, "E302", {"start": v(-26.71, -37.14) * mm, "end": v(-25.15, -38.22) * mm});
            skLineSegment(sketch, "E303", {"start": v(-25.15, -38.22) * mm, "end": v(-23.56, -36.7) * mm});
            skLineSegment(sketch, "E304", {"start": v(-23.56, -36.7) * mm, "end": v(-20.95, -38.25) * mm});
            skLineSegment(sketch, "E305", {"start": v(-20.95, -38.25) * mm, "end": v(-21.53, -40.37) * mm});
            skLineSegment(sketch, "E306", {"start": v(-21.53, -40.37) * mm, "end": v(-19.83, -41.23) * mm});
            skLineSegment(sketch, "E307", {"start": v(-19.83, -41.23) * mm, "end": v(-18.46, -39.52) * mm});
            skLineSegment(sketch, "E308", {"start": v(-18.46, -39.52) * mm, "end": v(-15.67, -40.7) * mm});
            skLineSegment(sketch, "E309", {"start": v(-15.67, -40.7) * mm, "end": v(-15.95, -42.88) * mm});
            skLineSegment(sketch, "E310", {"start": v(-15.95, -42.88) * mm, "end": v(-14.16, -43.5) * mm});
            skLineSegment(sketch, "E311", {"start": v(-14.16, -43.5) * mm, "end": v(-13.04, -41.63) * mm});
            skLineSegment(sketch, "E312", {"start": v(-13.04, -41.63) * mm, "end": v(-10.1, -42.43) * mm});
            skLineSegment(sketch, "E313", {"start": v(-10.1, -42.43) * mm, "end": v(-10.1, -44.62) * mm});
            skLineSegment(sketch, "E314", {"start": v(-10.1, -44.62) * mm, "end": v(-8.24, -45) * mm});
            skLineSegment(sketch, "E315", {"start": v(-8.24, -45) * mm, "end": v(-7.37, -43) * mm});
            skLineSegment(sketch, "E316", {"start": v(-7.37, -43) * mm, "end": v(-4.36, -43.4) * mm});
            skLineSegment(sketch, "E317", {"start": v(-4.36, -43.4) * mm, "end": v(-4.06, -45.58) * mm});
            skLineSegment(sketch, "E318", {"start": v(-4.06, -45.58) * mm, "end": v(-2.17, -45.7) * mm});
            skLineSegment(sketch, "E319", {"start": v(-2.17, -45.7) * mm, "end": v(-1.58, -43.59) * mm});
            skLineSegment(sketch, "E320", {"start": v(-1.58, -43.59) * mm, "end": v(1.46, -43.59) * mm});
            skLineSegment(sketch, "E321", {"start": v(1.46, -43.59) * mm, "end": v(2.04, -45.7) * mm});
            skLineSegment(sketch, "E322", {"start": v(2.04, -45.7) * mm, "end": v(3.93, -45.58) * mm});
            skLineSegment(sketch, "E323", {"start": v(3.93, -45.58) * mm, "end": v(4.24, -43.4) * mm});
            skLineSegment(sketch, "E324", {"start": v(4.24, -43.4) * mm, "end": v(7.25, -43.02) * mm});
            skLineSegment(sketch, "E325", {"start": v(7.25, -43.02) * mm, "end": v(8.11, -45.03) * mm});
            skLineSegment(sketch, "E326", {"start": v(8.11, -45.03) * mm, "end": v(9.97, -44.66) * mm});
            skLineSegment(sketch, "E327", {"start": v(9.97, -44.66) * mm, "end": v(9.99, -42.46) * mm});
            skLineSegment(sketch, "E328", {"start": v(9.99, -42.46) * mm, "end": v(12.92, -41.67) * mm});
            skLineSegment(sketch, "E329", {"start": v(12.92, -41.67) * mm, "end": v(14.04, -43.56) * mm});
            skLineSegment(sketch, "E330", {"start": v(14.04, -43.56) * mm, "end": v(15.83, -42.93) * mm});
            skLineSegment(sketch, "E331", {"start": v(15.83, -42.93) * mm, "end": v(15.56, -40.76) * mm});
            skLineSegment(sketch, "E332", {"start": v(15.56, -40.76) * mm, "end": v(18.35, -39.58) * mm});
            skLineSegment(sketch, "E333", {"start": v(18.35, -39.58) * mm, "end": v(19.72, -41.29) * mm});
            skLineSegment(sketch, "E334", {"start": v(19.72, -41.29) * mm, "end": v(21.41, -40.43) * mm});
            skLineSegment(sketch, "E335", {"start": v(21.41, -40.43) * mm, "end": v(20.85, -38.32) * mm});
            skLineSegment(sketch, "E336", {"start": v(20.85, -38.32) * mm, "end": v(23.46, -36.77) * mm});
            skLineSegment(sketch, "E337", {"start": v(23.46, -36.77) * mm, "end": v(25.04, -38.29) * mm});
            skLineSegment(sketch, "E338", {"start": v(25.04, -38.29) * mm, "end": v(26.6, -37.22) * mm});
            skLineSegment(sketch, "E339", {"start": v(26.6, -37.22) * mm, "end": v(25.76, -35.2) * mm});
            skLineSegment(sketch, "E340", {"start": v(25.76, -35.2) * mm, "end": v(28.15, -33.32) * mm});
            skLineSegment(sketch, "E341", {"start": v(28.15, -33.32) * mm, "end": v(29.92, -34.6) * mm});
            skLineSegment(sketch, "E342", {"start": v(29.92, -34.6) * mm, "end": v(31.33, -33.34) * mm});
            skLineSegment(sketch, "E343", {"start": v(31.33, -33.34) * mm, "end": v(30.22, -31.45) * mm});
            skLineSegment(sketch, "E344", {"start": v(30.22, -31.45) * mm, "end": v(32.33, -29.27) * mm});
            skLineSegment(sketch, "E345", {"start": v(32.33, -29.27) * mm, "end": v(34.26, -30.32) * mm});
            skLineSegment(sketch, "E346", {"start": v(34.26, -30.32) * mm, "end": v(35.49, -28.87) * mm});
            skLineSegment(sketch, "E347", {"start": v(35.49, -28.87) * mm, "end": v(34.14, -27.14) * mm});
            skLineSegment(sketch, "E348", {"start": v(34.14, -27.14) * mm, "end": v(35.95, -24.7) * mm});
            skLineSegment(sketch, "E349", {"start": v(35.95, -24.7) * mm, "end": v(38, -25.48) * mm});
            skLineSegment(sketch, "E350", {"start": v(38, -25.48) * mm, "end": v(39.01, -23.88) * mm});
            skLineSegment(sketch, "E351", {"start": v(39.01, -23.88) * mm, "end": v(37.45, -22.35) * mm});
            skLineSegment(sketch, "E352", {"start": v(37.45, -22.35) * mm, "end": v(38.92, -19.7) * mm});
            skLineSegment(sketch, "E353", {"start": v(38.92, -19.7) * mm, "end": v(41.05, -20.2) * mm});
            skLineSegment(sketch, "E354", {"start": v(41.05, -20.2) * mm, "end": v(41.85, -18.47) * mm});
            skLineSegment(sketch, "E355", {"start": v(41.85, -18.47) * mm, "end": v(40.1, -17.16) * mm});
            skLineSegment(sketch, "E356", {"start": v(40.1, -17.16) * mm, "end": v(41.2, -14.33) * mm});
            skLineSegment(sketch, "E357", {"start": v(41.2, -14.33) * mm, "end": v(43.37, -14.54) * mm});
            skLineSegment(sketch, "E358", {"start": v(43.37, -14.54) * mm, "end": v(43.94, -12.73) * mm});
            skLineSegment(sketch, "E359", {"start": v(43.94, -12.73) * mm, "end": v(42.02, -11.67) * mm});
            skLineSegment(sketch, "E360", {"start": v(42.02, -11.67) * mm, "end": v(42.73, -8.71) * mm});
            skLineSegment(sketch, "E361", {"start": v(42.73, -8.71) * mm, "end": v(44.93, -8.63) * mm});
            skLineSegment(sketch, "E362", {"start": v(44.93, -8.63) * mm, "end": v(45.24, -6.76) * mm});
            skLineSegment(sketch, "E363", {"start": v(45.24, -6.76) * mm, "end": v(43.2, -5.96) * mm});
            skLineSegment(sketch, "E364", {"start": v(43.2, -5.96) * mm, "end": v(43.5, -2.94) * mm});
            skLineSegment(sketch, "E365", {"start": v(43.5, -2.94) * mm, "end": v(45.66, -2.57) * mm});
            skLineSegment(sketch, "E366", {"start": v(45.66, -2.57) * mm, "end": v(45.72, -0.67) * mm});
            skLineSegment(sketch, "E367", {"start": v(45.72, -0.67) * mm, "end": v(43.6, -0.15) * mm});
            skPoint(sketch, "E368", {"position": v(0, 0) * mm});
            skCircle(sketch, "E369", {"center": v(0, 0) * mm, "radius": 0.72 * mm});
            skSolve(sketch);
        }
        {
            var Q0;
            Q0=makeQuery(id+"F0.imprint","IMPRINT",FACE,{"disambiguationData":[TD([[makeQuery(id+"F0.imprint","IMPRINT",EDGE,{"derivedFrom":sQuery(id+"F0.wireOp",EDGE,"E0")}),-1.0]])]});
            var Q1;
            Q1=makeQuery(id+"F0.imprint","IMPRINT",FACE,{"disambiguationData":[TD([[makeQuery(id+"F0.imprint","IMPRINT",EDGE,{"derivedFrom":sQuery(id+"F0.wireOp",EDGE,"E0")}),1.0]])]});
            extrude(context, id + "F1", {"entities" : qUnion([Q0, Q1]), "depth" : 6 * mm});
        }
        {
            var Q0;
            Q0=makeQuery(id+"F0.imprint","IMPRINT",FACE,{"disambiguationData":[TD([[makeQuery(id+"F0.imprint","IMPRINT",EDGE,{"derivedFrom":sQuery(id+"F0.wireOp",EDGE,"E0")}),1.0]])]});
            extrude(context, id + "F2", {"entities" : qUnion([Q0]), "operationType" : NewBodyOperationType.ADD, "depth" : 12 * mm});
        }
        {
            var Q0;
            Q0=makeQuery(id+"F2.opExtrude","CAP_FACE",FACE,{"disambiguationData":[OSD([sQuery(id+"F0.wireOp",EDGE,"E0"),sQuery(id+"F0.wireOp",EDGE,"E1"),sQuery(id+"F0.wireOp",EDGE,"E2"),sQuery(id+"F0.wireOp",EDGE,"E3"),sQuery(id+"F0.wireOp",EDGE,"E4"),sQuery(id+"F0.wireOp",EDGE,"E5"),sQuery(id+"F0.wireOp",EDGE,"E6"),sQuery(id+"F0.wireOp",EDGE,"E7"),sQuery(id+"F0.wireOp",EDGE,"E8"),sQuery(id+"F0.wireOp",EDGE,"E9"),sQuery(id+"F0.wireOp",EDGE,"E10"),sQuery(id+"F0.wireOp",EDGE,"E11"),sQuery(id+"F0.wireOp",EDGE,"E12"),sQuery(id+"F0.wireOp",EDGE,"E13"),sQuery(id+"F0.wireOp",EDGE,"E14"),sQuery(id+"F0.wireOp",EDGE,"E15"),sQuery(id+"F0.wireOp",EDGE,"E16"),sQuery(id+"F0.wireOp",EDGE,"E17"),sQuery(id+"F0.wireOp",EDGE,"E18"),sQuery(id+"F0.wireOp",EDGE,"E19"),sQuery(id+"F0.wireOp",EDGE,"E20"),sQuery(id+"F0.wireOp",EDGE,"E21"),sQuery(id+"F0.wireOp",EDGE,"E22"),sQuery(id+"F0.wireOp",EDGE,"E23"),sQuery(id+"F0.wireOp",EDGE,"E24"),sQuery(id+"F0.wireOp",EDGE,"E25"),sQuery(id+"F0.wireOp",EDGE,"E26"),sQuery(id+"F0.wireOp",EDGE,"E27"),sQuery(id+"F0.wireOp",EDGE,"E28"),sQuery(id+"F0.wireOp",EDGE,"E29"),sQuery(id+"F0.wireOp",EDGE,"E30"),sQuery(id+"F0.wireOp",EDGE,"E31"),sQuery(id+"F0.wireOp",EDGE,"E32"),sQuery(id+"F0.wireOp",EDGE,"E33"),sQuery(id+"F0.wireOp",EDGE,"E34"),sQuery(id+"F0.wireOp",EDGE,"E35"),sQuery(id+"F0.wireOp",EDGE,"E36"),sQuery(id+"F0.wireOp",EDGE,"E37"),sQuery(id+"F0.wireOp",EDGE,"E38"),sQuery(id+"F0.wireOp",EDGE,"E39"),sQuery(id+"F0.wireOp",EDGE,"E40"),sQuery(id+"F0.wireOp",EDGE,"E41"),sQuery(id+"F0.wireOp",EDGE,"E42"),sQuery(id+"F0.wireOp",EDGE,"E43"),sQuery(id+"F0.wireOp",EDGE,"E44"),sQuery(id+"F0.wireOp",EDGE,"E45"),sQuery(id+"F0.wireOp",EDGE,"E46"),sQuery(id+"F0.wireOp",EDGE,"E47"),sQuery(id+"F0.wireOp",EDGE,"E48"),sQuery(id+"F0.wireOp",EDGE,"E49"),sQuery(id+"F0.wireOp",EDGE,"E50"),sQuery(id+"F0.wireOp",EDGE,"E51"),sQuery(id+"F0.wireOp",EDGE,"E52"),sQuery(id+"F0.wireOp",EDGE,"E53"),sQuery(id+"F0.wireOp",EDGE,"E54"),sQuery(id+"F0.wireOp",EDGE,"E55"),sQuery(id+"F0.wireOp",EDGE,"E56"),sQuery(id+"F0.wireOp",EDGE,"E57"),sQuery(id+"F0.wireOp",EDGE,"E58"),sQuery(id+"F0.wireOp",EDGE,"E59"),sQuery(id+"F0.wireOp",EDGE,"E60"),sQuery(id+"F0.wireOp",EDGE,"E61"),sQuery(id+"F0.wireOp",EDGE,"E62"),sQuery(id+"F0.wireOp",EDGE,"E63"),sQuery(id+"F0.wireOp",EDGE,"E64"),sQuery(id+"F0.wireOp",EDGE,"E65"),sQuery(id+"F0.wireOp",EDGE,"E66"),sQuery(id+"F0.wireOp",EDGE,"E67"),sQuery(id+"F0.wireOp",EDGE,"E68"),sQuery(id+"F0.wireOp",EDGE,"E69"),sQuery(id+"F0.wireOp",EDGE,"E70"),sQuery(id+"F0.wireOp",EDGE,"E71"),sQuery(id+"F0.wireOp",EDGE,"E72"),sQuery(id+"F0.wireOp",EDGE,"E73"),sQuery(id+"F0.wireOp",EDGE,"E74"),sQuery(id+"F0.wireOp",EDGE,"E75"),sQuery(id+"F0.wireOp",EDGE,"E76"),sQuery(id+"F0.wireOp",EDGE,"E77"),sQuery(id+"F0.wireOp",EDGE,"E78"),sQuery(id+"F0.wireOp",EDGE,"E79"),sQuery(id+"F0.wireOp",EDGE,"E80"),sQuery(id+"F0.wireOp",EDGE,"E81"),sQuery(id+"F0.wireOp",EDGE,"E82"),sQuery(id+"F0.wireOp",EDGE,"E83"),sQuery(id+"F0.wireOp",EDGE,"E84"),sQuery(id+"F0.wireOp",EDGE,"E85"),sQuery(id+"F0.wireOp",EDGE,"E86"),sQuery(id+"F0.wireOp",EDGE,"E87"),sQuery(id+"F0.wireOp",EDGE,"E88"),sQuery(id+"F0.wireOp",EDGE,"E89"),sQuery(id+"F0.wireOp",EDGE,"E90"),sQuery(id+"F0.wireOp",EDGE,"E91"),sQuery(id+"F0.wireOp",EDGE,"E92"),sQuery(id+"F0.wireOp",EDGE,"E93"),sQuery(id+"F0.wireOp",EDGE,"E94"),sQuery(id+"F0.wireOp",EDGE,"E95"),sQuery(id+"F0.wireOp",EDGE,"E96"),sQuery(id+"F0.wireOp",EDGE,"E97"),sQuery(id+"F0.wireOp",EDGE,"E98"),sQuery(id+"F0.wireOp",EDGE,"E99"),sQuery(id+"F0.wireOp",EDGE,"E100"),sQuery(id+"F0.wireOp",EDGE,"E101"),sQuery(id+"F0.wireOp",EDGE,"E102"),sQuery(id+"F0.wireOp",EDGE,"E103"),sQuery(id+"F0.wireOp",EDGE,"E104"),sQuery(id+"F0.wireOp",EDGE,"E105"),sQuery(id+"F0.wireOp",EDGE,"E106"),sQuery(id+"F0.wireOp",EDGE,"E107"),sQuery(id+"F0.wireOp",EDGE,"E108"),sQuery(id+"F0.wireOp",EDGE,"E109"),sQuery(id+"F0.wireOp",EDGE,"E110"),sQuery(id+"F0.wireOp",EDGE,"E111"),sQuery(id+"F0.wireOp",EDGE,"E112"),sQuery(id+"F0.wireOp",EDGE,"E113"),sQuery(id+"F0.wireOp",EDGE,"E114"),sQuery(id+"F0.wireOp",EDGE,"E115"),sQuery(id+"F0.wireOp",EDGE,"E116"),sQuery(id+"F0.wireOp",EDGE,"E117"),sQuery(id+"F0.wireOp",EDGE,"E118"),sQuery(id+"F0.wireOp",EDGE,"E119"),sQuery(id+"F0.wireOp",EDGE,"E120"),sQuery(id+"F0.wireOp",EDGE,"E121"),sQuery(id+"F0.wireOp",EDGE,"E122"),sQuery(id+"F0.wireOp",EDGE,"E123"),sQuery(id+"F0.wireOp",EDGE,"E124"),sQuery(id+"F0.wireOp",EDGE,"E125"),sQuery(id+"F0.wireOp",EDGE,"E126"),sQuery(id+"F0.wireOp",EDGE,"E127"),sQuery(id+"F0.wireOp",EDGE,"E128"),sQuery(id+"F0.wireOp",EDGE,"E129"),sQuery(id+"F0.wireOp",EDGE,"E130"),sQuery(id+"F0.wireOp",EDGE,"E131"),sQuery(id+"F0.wireOp",EDGE,"E369")])],"isStart":false});
            cPlane(context, id + "F3", {"entities" : qUnion([Q0]), "cplaneType" : CPlaneType.OFFSET, "offset" : 0 * mm, "width" : 150 * mm, "height" : 150 * mm});
        }
        {
            var Q0;
            Q0=qCreatedBy(id+"F3.planeOp",FACE);
            var sketch = newSketch(context, id + "F4", { "sketchPlane" : qUnion([Q0])});
            skCircle(sketch, "E370", {"center": v(0, 0) * mm, "radius": 4.7 * mm});
            skSolve(sketch);
        }
        {
            var Q0;
            Q0=sQuery(id+"F0.wireOp",VERTEX,"E368");
            var Q1;
            Q1=makeQuery(id+"F1.opExtrude","SWEPT_BODY",BODY,{"disambiguationData":[OSD([sQuery(id+"F0.wireOp",EDGE,"E132"),sQuery(id+"F0.wireOp",EDGE,"E133"),sQuery(id+"F0.wireOp",EDGE,"E134"),sQuery(id+"F0.wireOp",EDGE,"E135"),sQuery(id+"F0.wireOp",EDGE,"E136"),sQuery(id+"F0.wireOp",EDGE,"E137"),sQuery(id+"F0.wireOp",EDGE,"E138"),sQuery(id+"F0.wireOp",EDGE,"E139"),sQuery(id+"F0.wireOp",EDGE,"E140"),sQuery(id+"F0.wireOp",EDGE,"E141"),sQuery(id+"F0.wireOp",EDGE,"E142"),sQuery(id+"F0.wireOp",EDGE,"E143"),sQuery(id+"F0.wireOp",EDGE,"E144"),sQuery(id+"F0.wireOp",EDGE,"E145"),sQuery(id+"F0.wireOp",EDGE,"E146"),sQuery(id+"F0.wireOp",EDGE,"E147"),sQuery(id+"F0.wireOp",EDGE,"E148"),sQuery(id+"F0.wireOp",EDGE,"E149"),sQuery(id+"F0.wireOp",EDGE,"E150"),sQuery(id+"F0.wireOp",EDGE,"E151"),sQuery(id+"F0.wireOp",EDGE,"E152"),sQuery(id+"F0.wireOp",EDGE,"E153"),sQuery(id+"F0.wireOp",EDGE,"E154"),sQuery(id+"F0.wireOp",EDGE,"E155"),sQuery(id+"F0.wireOp",EDGE,"E156"),sQuery(id+"F0.wireOp",EDGE,"E157"),sQuery(id+"F0.wireOp",EDGE,"E158"),sQuery(id+"F0.wireOp",EDGE,"E159"),sQuery(id+"F0.wireOp",EDGE,"E160"),sQuery(id+"F0.wireOp",EDGE,"E161"),sQuery(id+"F0.wireOp",EDGE,"E162"),sQuery(id+"F0.wireOp",EDGE,"E163"),sQuery(id+"F0.wireOp",EDGE,"E164"),sQuery(id+"F0.wireOp",EDGE,"E165"),sQuery(id+"F0.wireOp",EDGE,"E166"),sQuery(id+"F0.wireOp",EDGE,"E167"),sQuery(id+"F0.wireOp",EDGE,"E168"),sQuery(id+"F0.wireOp",EDGE,"E169"),sQuery(id+"F0.wireOp",EDGE,"E170"),sQuery(id+"F0.wireOp",EDGE,"E171"),sQuery(id+"F0.wireOp",EDGE,"E172"),sQuery(id+"F0.wireOp",EDGE,"E173"),sQuery(id+"F0.wireOp",EDGE,"E174"),sQuery(id+"F0.wireOp",EDGE,"E175"),sQuery(id+"F0.wireOp",EDGE,"E176"),sQuery(id+"F0.wireOp",EDGE,"E177"),sQuery(id+"F0.wireOp",EDGE,"E178"),sQuery(id+"F0.wireOp",EDGE,"E179"),sQuery(id+"F0.wireOp",EDGE,"E180"),sQuery(id+"F0.wireOp",EDGE,"E181"),sQuery(id+"F0.wireOp",EDGE,"E182"),sQuery(id+"F0.wireOp",EDGE,"E183"),sQuery(id+"F0.wireOp",EDGE,"E184"),sQuery(id+"F0.wireOp",EDGE,"E185"),sQuery(id+"F0.wireOp",EDGE,"E186"),sQuery(id+"F0.wireOp",EDGE,"E187"),sQuery(id+"F0.wireOp",EDGE,"E188"),sQuery(id+"F0.wireOp",EDGE,"E189"),sQuery(id+"F0.wireOp",EDGE,"E190"),sQuery(id+"F0.wireOp",EDGE,"E191"),sQuery(id+"F0.wireOp",EDGE,"E192"),sQuery(id+"F0.wireOp",EDGE,"E193"),sQuery(id+"F0.wireOp",EDGE,"E194"),sQuery(id+"F0.wireOp",EDGE,"E195"),sQuery(id+"F0.wireOp",EDGE,"E196"),sQuery(id+"F0.wireOp",EDGE,"E197"),sQuery(id+"F0.wireOp",EDGE,"E198"),sQuery(id+"F0.wireOp",EDGE,"E199"),sQuery(id+"F0.wireOp",EDGE,"E200"),sQuery(id+"F0.wireOp",EDGE,"E201"),sQuery(id+"F0.wireOp",EDGE,"E202"),sQuery(id+"F0.wireOp",EDGE,"E203"),sQuery(id+"F0.wireOp",EDGE,"E204"),sQuery(id+"F0.wireOp",EDGE,"E205"),sQuery(id+"F0.wireOp",EDGE,"E206"),sQuery(id+"F0.wireOp",EDGE,"E207"),sQuery(id+"F0.wireOp",EDGE,"E208"),sQuery(id+"F0.wireOp",EDGE,"E209"),sQuery(id+"F0.wireOp",EDGE,"E210"),sQuery(id+"F0.wireOp",EDGE,"E211"),sQuery(id+"F0.wireOp",EDGE,"E212"),sQuery(id+"F0.wireOp",EDGE,"E213"),sQuery(id+"F0.wireOp",EDGE,"E214"),sQuery(id+"F0.wireOp",EDGE,"E215"),sQuery(id+"F0.wireOp",EDGE,"E216"),sQuery(id+"F0.wireOp",EDGE,"E217"),sQuery(id+"F0.wireOp",EDGE,"E218"),sQuery(id+"F0.wireOp",EDGE,"E219"),sQuery(id+"F0.wireOp",EDGE,"E220"),sQuery(id+"F0.wireOp",EDGE,"E221"),sQuery(id+"F0.wireOp",EDGE,"E222"),sQuery(id+"F0.wireOp",EDGE,"E223"),sQuery(id+"F0.wireOp",EDGE,"E224"),sQuery(id+"F0.wireOp",EDGE,"E225"),sQuery(id+"F0.wireOp",EDGE,"E226"),sQuery(id+"F0.wireOp",EDGE,"E227"),sQuery(id+"F0.wireOp",EDGE,"E228"),sQuery(id+"F0.wireOp",EDGE,"E229"),sQuery(id+"F0.wireOp",EDGE,"E230"),sQuery(id+"F0.wireOp",EDGE,"E231"),sQuery(id+"F0.wireOp",EDGE,"E232"),sQuery(id+"F0.wireOp",EDGE,"E233"),sQuery(id+"F0.wireOp",EDGE,"E234"),sQuery(id+"F0.wireOp",EDGE,"E235"),sQuery(id+"F0.wireOp",EDGE,"E236"),sQuery(id+"F0.wireOp",EDGE,"E237"),sQuery(id+"F0.wireOp",EDGE,"E238"),sQuery(id+"F0.wireOp",EDGE,"E239"),sQuery(id+"F0.wireOp",EDGE,"E240"),sQuery(id+"F0.wireOp",EDGE,"E241"),sQuery(id+"F0.wireOp",EDGE,"E242"),sQuery(id+"F0.wireOp",EDGE,"E243"),sQuery(id+"F0.wireOp",EDGE,"E244"),sQuery(id+"F0.wireOp",EDGE,"E245"),sQuery(id+"F0.wireOp",EDGE,"E246"),sQuery(id+"F0.wireOp",EDGE,"E247"),sQuery(id+"F0.wireOp",EDGE,"E248"),sQuery(id+"F0.wireOp",EDGE,"E249"),sQuery(id+"F0.wireOp",EDGE,"E250"),sQuery(id+"F0.wireOp",EDGE,"E251"),sQuery(id+"F0.wireOp",EDGE,"E252"),sQuery(id+"F0.wireOp",EDGE,"E253"),sQuery(id+"F0.wireOp",EDGE,"E254"),sQuery(id+"F0.wireOp",EDGE,"E255"),sQuery(id+"F0.wireOp",EDGE,"E256"),sQuery(id+"F0.wireOp",EDGE,"E257"),sQuery(id+"F0.wireOp",EDGE,"E258"),sQuery(id+"F0.wireOp",EDGE,"E259"),sQuery(id+"F0.wireOp",EDGE,"E260"),sQuery(id+"F0.wireOp",EDGE,"E261"),sQuery(id+"F0.wireOp",EDGE,"E262"),sQuery(id+"F0.wireOp",EDGE,"E263"),sQuery(id+"F0.wireOp",EDGE,"E264"),sQuery(id+"F0.wireOp",EDGE,"E265"),sQuery(id+"F0.wireOp",EDGE,"E266"),sQuery(id+"F0.wireOp",EDGE,"E267"),sQuery(id+"F0.wireOp",EDGE,"E268"),sQuery(id+"F0.wireOp",EDGE,"E269"),sQuery(id+"F0.wireOp",EDGE,"E270"),sQuery(id+"F0.wireOp",EDGE,"E271"),sQuery(id+"F0.wireOp",EDGE,"E272"),sQuery(id+"F0.wireOp",EDGE,"E273"),sQuery(id+"F0.wireOp",EDGE,"E274"),sQuery(id+"F0.wireOp",EDGE,"E275"),sQuery(id+"F0.wireOp",EDGE,"E276"),sQuery(id+"F0.wireOp",EDGE,"E277"),sQuery(id+"F0.wireOp",EDGE,"E278"),sQuery(id+"F0.wireOp",EDGE,"E279"),sQuery(id+"F0.wireOp",EDGE,"E280"),sQuery(id+"F0.wireOp",EDGE,"E281"),sQuery(id+"F0.wireOp",EDGE,"E282"),sQuery(id+"F0.wireOp",EDGE,"E283"),sQuery(id+"F0.wireOp",EDGE,"E284"),sQuery(id+"F0.wireOp",EDGE,"E285"),sQuery(id+"F0.wireOp",EDGE,"E286"),sQuery(id+"F0.wireOp",EDGE,"E287"),sQuery(id+"F0.wireOp",EDGE,"E288"),sQuery(id+"F0.wireOp",EDGE,"E289"),sQuery(id+"F0.wireOp",EDGE,"E290"),sQuery(id+"F0.wireOp",EDGE,"E291"),sQuery(id+"F0.wireOp",EDGE,"E292"),sQuery(id+"F0.wireOp",EDGE,"E293"),sQuery(id+"F0.wireOp",EDGE,"E294"),sQuery(id+"F0.wireOp",EDGE,"E295"),sQuery(id+"F0.wireOp",EDGE,"E296"),sQuery(id+"F0.wireOp",EDGE,"E297"),sQuery(id+"F0.wireOp",EDGE,"E298"),sQuery(id+"F0.wireOp",EDGE,"E299"),sQuery(id+"F0.wireOp",EDGE,"E300"),sQuery(id+"F0.wireOp",EDGE,"E301"),sQuery(id+"F0.wireOp",EDGE,"E302"),sQuery(id+"F0.wireOp",EDGE,"E303"),sQuery(id+"F0.wireOp",EDGE,"E304"),sQuery(id+"F0.wireOp",EDGE,"E305"),sQuery(id+"F0.wireOp",EDGE,"E306"),sQuery(id+"F0.wireOp",EDGE,"E307"),sQuery(id+"F0.wireOp",EDGE,"E308"),sQuery(id+"F0.wireOp",EDGE,"E309"),sQuery(id+"F0.wireOp",EDGE,"E310"),sQuery(id+"F0.wireOp",EDGE,"E311"),sQuery(id+"F0.wireOp",EDGE,"E312"),sQuery(id+"F0.wireOp",EDGE,"E313"),sQuery(id+"F0.wireOp",EDGE,"E314"),sQuery(id+"F0.wireOp",EDGE,"E315"),sQuery(id+"F0.wireOp",EDGE,"E316"),sQuery(id+"F0.wireOp",EDGE,"E317"),sQuery(id+"F0.wireOp",EDGE,"E318"),sQuery(id+"F0.wireOp",EDGE,"E319"),sQuery(id+"F0.wireOp",EDGE,"E320"),sQuery(id+"F0.wireOp",EDGE,"E321"),sQuery(id+"F0.wireOp",EDGE,"E322"),sQuery(id+"F0.wireOp",EDGE,"E323"),sQuery(id+"F0.wireOp",EDGE,"E324"),sQuery(id+"F0.wireOp",EDGE,"E325"),sQuery(id+"F0.wireOp",EDGE,"E326"),sQuery(id+"F0.wireOp",EDGE,"E327"),sQuery(id+"F0.wireOp",EDGE,"E328"),sQuery(id+"F0.wireOp",EDGE,"E329"),sQuery(id+"F0.wireOp",EDGE,"E330"),sQuery(id+"F0.wireOp",EDGE,"E331"),sQuery(id+"F0.wireOp",EDGE,"E332"),sQuery(id+"F0.wireOp",EDGE,"E333"),sQuery(id+"F0.wireOp",EDGE,"E334"),sQuery(id+"F0.wireOp",EDGE,"E335"),sQuery(id+"F0.wireOp",EDGE,"E336"),sQuery(id+"F0.wireOp",EDGE,"E337"),sQuery(id+"F0.wireOp",EDGE,"E338"),sQuery(id+"F0.wireOp",EDGE,"E339"),sQuery(id+"F0.wireOp",EDGE,"E340"),sQuery(id+"F0.wireOp",EDGE,"E341"),sQuery(id+"F0.wireOp",EDGE,"E342"),sQuery(id+"F0.wireOp",EDGE,"E343"),sQuery(id+"F0.wireOp",EDGE,"E344"),sQuery(id+"F0.wireOp",EDGE,"E345"),sQuery(id+"F0.wireOp",EDGE,"E346"),sQuery(id+"F0.wireOp",EDGE,"E347"),sQuery(id+"F0.wireOp",EDGE,"E348"),sQuery(id+"F0.wireOp",EDGE,"E349"),sQuery(id+"F0.wireOp",EDGE,"E350"),sQuery(id+"F0.wireOp",EDGE,"E351"),sQuery(id+"F0.wireOp",EDGE,"E352"),sQuery(id+"F0.wireOp",EDGE,"E353"),sQuery(id+"F0.wireOp",EDGE,"E354"),sQuery(id+"F0.wireOp",EDGE,"E355"),sQuery(id+"F0.wireOp",EDGE,"E356"),sQuery(id+"F0.wireOp",EDGE,"E357"),sQuery(id+"F0.wireOp",EDGE,"E358"),sQuery(id+"F0.wireOp",EDGE,"E359"),sQuery(id+"F0.wireOp",EDGE,"E360"),sQuery(id+"F0.wireOp",EDGE,"E361"),sQuery(id+"F0.wireOp",EDGE,"E362"),sQuery(id+"F0.wireOp",EDGE,"E363"),sQuery(id+"F0.wireOp",EDGE,"E364"),sQuery(id+"F0.wireOp",EDGE,"E365"),sQuery(id+"F0.wireOp",EDGE,"E366"),sQuery(id+"F0.wireOp",EDGE,"E367"),sQuery(id+"F0.wireOp",EDGE,"E369")])]});
            hole(context, id + "F5", {"style" : HoleStyle.SIMPLE, "holeDiameter" : 4 * mm, "endStyle" : HoleEndStyle.THROUGH, "oppositeDirection" : true, "locations" : qUnion([Q0]), "scope" : qUnion([Q1])});
        }
    });
